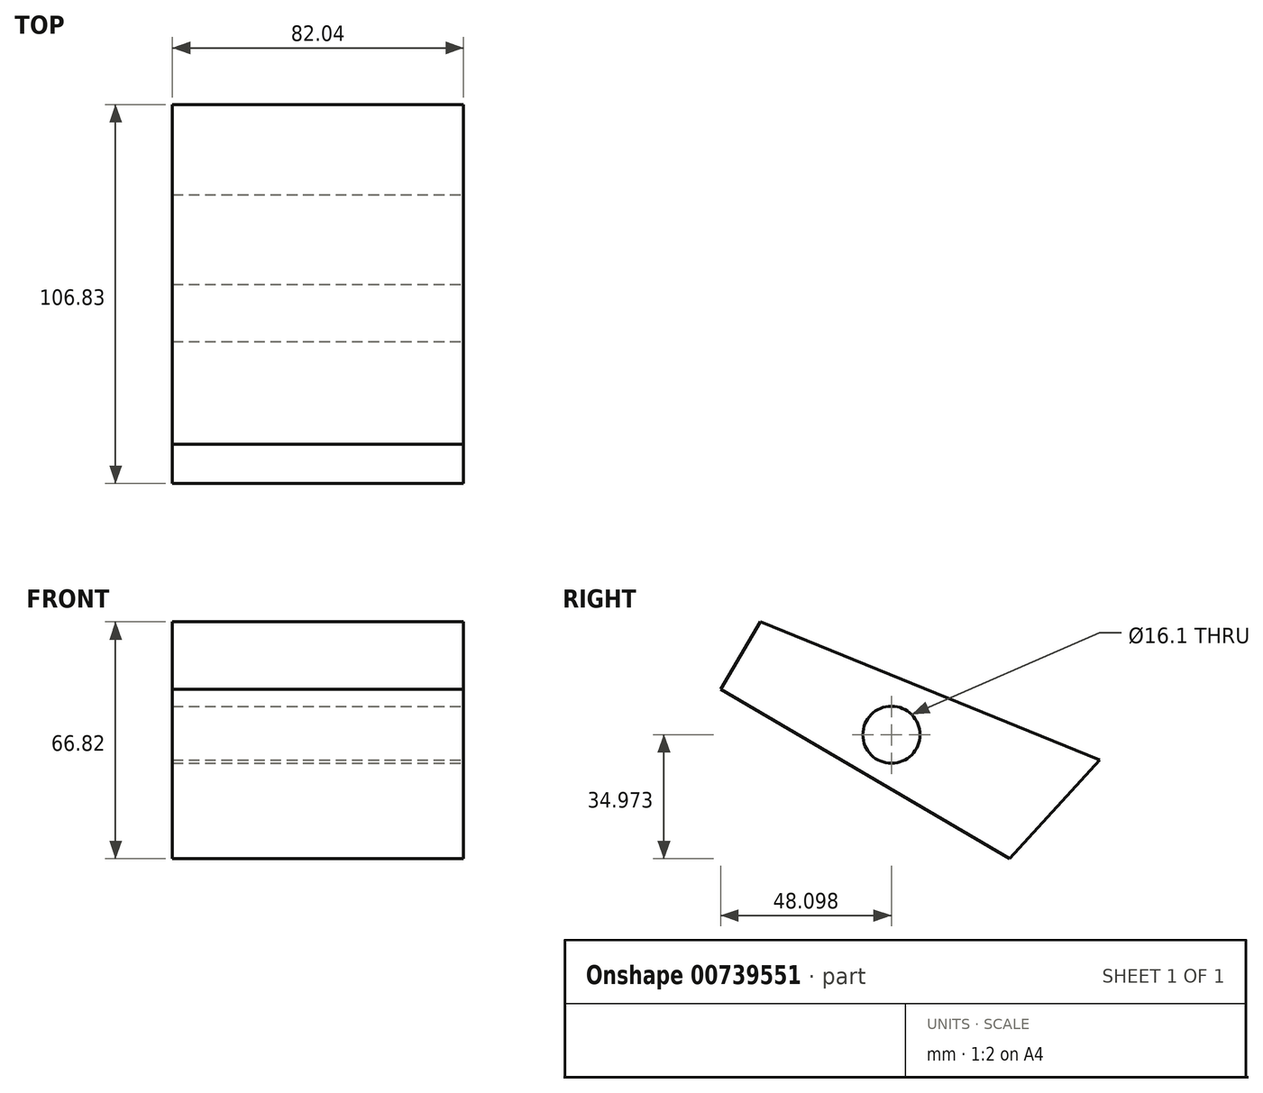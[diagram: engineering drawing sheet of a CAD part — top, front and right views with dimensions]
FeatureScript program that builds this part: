
annotation { "Feature Type Name" : "Feature", "Feature Type Description" : "" }
export const myFeature = defineFeature(function(context is Context, id is Id, definition is map)
    precondition{}
    {
        {
            var Q0;
            Q0=qCreatedBy(makeId("Right.planeOp"),FACE);
            var sketch = newSketch(context, id + "F0", { "sketchPlane" : qUnion([Q0])});
            skLineSegment(sketch, "E0", {"start": v(-106.83, 47.8) * mm, "end": v(-25.44, 0) * mm});
            skLineSegment(sketch, "E1", {"start": v(-25.44, 0) * mm, "end": v(0, 27.88) * mm});
            skLineSegment(sketch, "E2", {"start": v(0, 27.88) * mm, "end": v(-95.73, 66.82) * mm});
            skLineSegment(sketch, "E3", {"start": v(-95.73, 66.82) * mm, "end": v(-106.83, 47.8) * mm});
            skCircle(sketch, "E4", {"center": v(-58.73, 34.97) * mm, "radius": 8.05 * mm});
            skSolve(sketch);
        }
        {
            var Q0;
            Q0 = qSketchRegion(id + "F0", true);
            extrude(context, id + "F1", {"entities" : qUnion([Q0]), "oppositeDirection" : true, "depth" : 82.04 * mm, "offsetDistance" : 25.4 * mm});
        }
    });
